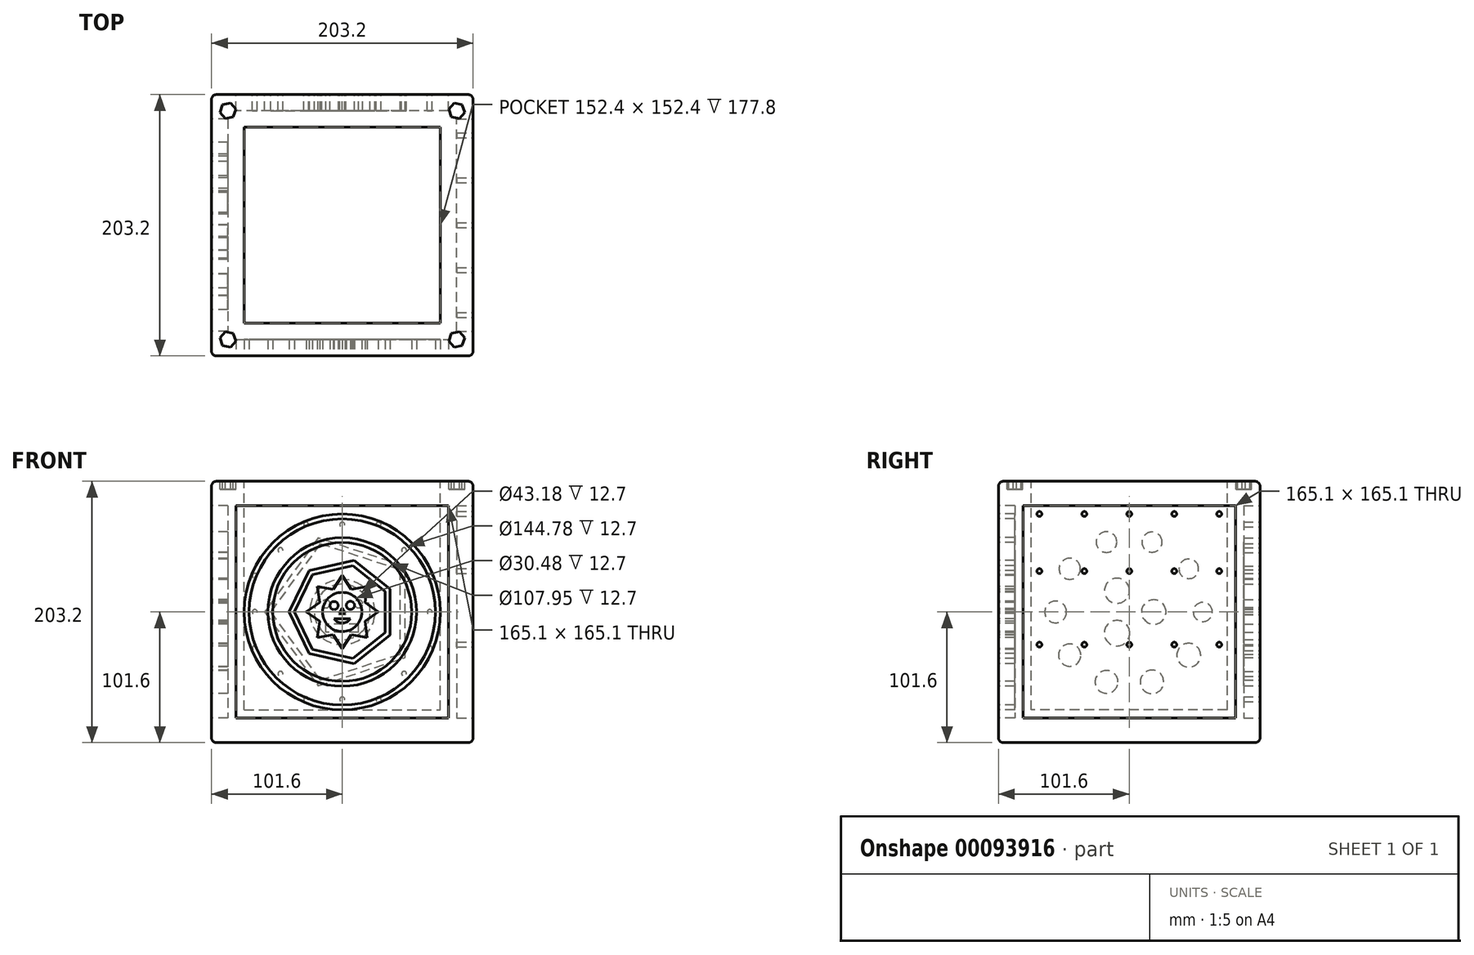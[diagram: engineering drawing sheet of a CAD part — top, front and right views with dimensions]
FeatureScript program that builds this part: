
annotation { "Feature Type Name" : "Feature", "Feature Type Description" : "" }
export const myFeature = defineFeature(function(context is Context, id is Id, definition is map)
    precondition{}
    {
        {
            var Q0;
            Q0=qCreatedBy(makeId("Front.planeOp"),FACE);
            var sketch = newSketch(context, id + "F0", { "sketchPlane" : qUnion([Q0])});
            skLineSegment(sketch, "E0.bottom", {"start": v(-101.6, 101.6) * mm, "end": v(101.6, 101.6) * mm});
            skLineSegment(sketch, "E0.top", {"start": v(-101.6, -101.6) * mm, "end": v(101.6, -101.6) * mm});
            skLineSegment(sketch, "E0.left", {"start": v(-101.6, 101.6) * mm, "end": v(-101.6, -101.6) * mm});
            skLineSegment(sketch, "E0.right", {"start": v(101.6, 101.6) * mm, "end": v(101.6, -101.6) * mm});
            skPoint(sketch, "E0.middle", {"position": v(0, 0) * mm});
            skSolve(sketch);
        }
        {
            var Q0;
            Q0 = qSketchRegion(id + "F0", true);
            extrude(context, id + "F1", {"entities" : qUnion([Q0]), "endBound" : BoundingType.SYMMETRIC, "depth" : 203.2 * mm});
        }
        {
            var Q0;
            Q0=makeQuery(id+"F1.opExtrude","SWEPT_FACE",FACE,{"disambiguationData":[OSD([sQuery(id+"F0.wireOp",EDGE,"E0.bottom")])]});
            var sketch = newSketch(context, id + "F2", { "sketchPlane" : qUnion([Q0])});
            skPoint(sketch, "E1.middle", {"position": v(0, 0) * mm});
            skLineSegment(sketch, "E2.bottom", {"start": v(-76.2, 76.2) * mm, "end": v(76.2, 76.2) * mm});
            skLineSegment(sketch, "E2.top", {"start": v(-76.2, -76.2) * mm, "end": v(76.2, -76.2) * mm});
            skLineSegment(sketch, "E2.left", {"start": v(-76.2, 76.2) * mm, "end": v(-76.2, -76.2) * mm});
            skLineSegment(sketch, "E2.right", {"start": v(76.2, 76.2) * mm, "end": v(76.2, -76.2) * mm});
            skLineSegment(sketch, "E3.bottom", {"start": v(-76.2, 76.2) * mm, "end": v(-101.6, 76.2) * mm, "construction": true});
            skLineSegment(sketch, "E3.top", {"start": v(-76.2, 101.6) * mm, "end": v(-101.6, 101.6) * mm, "construction": true});
            skLineSegment(sketch, "E3.left", {"start": v(-76.2, 76.2) * mm, "end": v(-76.2, 101.6) * mm, "construction": true});
            skLineSegment(sketch, "E3.right", {"start": v(-101.6, 76.2) * mm, "end": v(-101.6, 101.6) * mm, "construction": true});
            skLineSegment(sketch, "E4.bottom", {"start": v(76.2, 76.2) * mm, "end": v(101.6, 76.2) * mm, "construction": true});
            skLineSegment(sketch, "E4.top", {"start": v(76.2, 101.6) * mm, "end": v(101.6, 101.6) * mm, "construction": true});
            skLineSegment(sketch, "E4.left", {"start": v(76.2, 76.2) * mm, "end": v(76.2, 101.6) * mm, "construction": true});
            skLineSegment(sketch, "E4.right", {"start": v(101.6, 76.2) * mm, "end": v(101.6, 101.6) * mm, "construction": true});
            skLineSegment(sketch, "E5.bottom", {"start": v(-76.2, -76.2) * mm, "end": v(-101.6, -76.2) * mm, "construction": true});
            skLineSegment(sketch, "E5.top", {"start": v(-76.2, -101.6) * mm, "end": v(-101.6, -101.6) * mm, "construction": true});
            skLineSegment(sketch, "E5.left", {"start": v(-76.2, -76.2) * mm, "end": v(-76.2, -101.6) * mm, "construction": true});
            skLineSegment(sketch, "E5.right", {"start": v(-101.6, -76.2) * mm, "end": v(-101.6, -101.6) * mm, "construction": true});
            skLineSegment(sketch, "E6.bottom", {"start": v(76.2, -76.2) * mm, "end": v(101.6, -76.2) * mm, "construction": true});
            skLineSegment(sketch, "E6.top", {"start": v(76.2, -101.6) * mm, "end": v(101.6, -101.6) * mm, "construction": true});
            skLineSegment(sketch, "E6.left", {"start": v(76.2, -76.2) * mm, "end": v(76.2, -101.6) * mm, "construction": true});
            skLineSegment(sketch, "E6.right", {"start": v(101.6, -76.2) * mm, "end": v(101.6, -101.6) * mm, "construction": true});
            skLineSegment(sketch, "E7", {"start": v(-101.6, 76.2) * mm, "end": v(-76.2, 101.6) * mm, "construction": true});
            skCircle(sketch, "E8.cCircle", {"center": v(-88.9, 88.9) * mm, "radius": 5.5 * mm, "construction": true});
            skLineSegment(sketch, "E8.0", {"start": v(-84.72, 84.12) * mm, "end": v(-90.95, 82.9) * mm});
            skLineSegment(sketch, "E8.1", {"start": v(-90.95, 82.9) * mm, "end": v(-95.13, 87.68) * mm});
            skLineSegment(sketch, "E8.2", {"start": v(-95.13, 87.68) * mm, "end": v(-93.08, 93.68) * mm});
            skLineSegment(sketch, "E8.3", {"start": v(-93.08, 93.68) * mm, "end": v(-86.85, 94.9) * mm});
            skLineSegment(sketch, "E8.4", {"start": v(-86.85, 94.9) * mm, "end": v(-82.67, 90.12) * mm});
            skLineSegment(sketch, "E8.5", {"start": v(-82.67, 90.12) * mm, "end": v(-84.72, 84.12) * mm});
            skPoint(sketch, "E8.0.midPoint", {"position": v(-87.84, 83.5) * mm});
            skLineSegment(sketch, "E9", {"start": v(0, 101.6) * mm, "end": v(0, -101.6) * mm, "construction": true});
            skLineSegment(sketch, "E10", {"start": v(-101.6, 0) * mm, "end": v(101.6, 0) * mm, "construction": true});
            skLineSegment(sketch, "E11.MirrorCS", {"start": v(0, -101.6) * mm, "end": v(0, 101.6) * mm, "construction": true});
            skLineSegment(sketch, "E12.MirrorCS", {"start": v(-90.95, -82.9) * mm, "end": v(-95.13, -87.68) * mm});
            skLineSegment(sketch, "E13.MirrorCS", {"start": v(-95.13, -87.68) * mm, "end": v(-93.08, -93.68) * mm});
            skLineSegment(sketch, "E14.MirrorCS", {"start": v(-93.08, -93.68) * mm, "end": v(-86.85, -94.9) * mm});
            skLineSegment(sketch, "E15.MirrorCS", {"start": v(-86.85, -94.9) * mm, "end": v(-82.67, -90.12) * mm});
            skLineSegment(sketch, "E16.MirrorCS", {"start": v(-82.67, -90.12) * mm, "end": v(-84.72, -84.12) * mm});
            skLineSegment(sketch, "E17.MirrorCS", {"start": v(-84.72, -84.12) * mm, "end": v(-90.95, -82.9) * mm});
            skLineSegment(sketch, "E18.MirrorCS", {"start": v(82.67, 90.12) * mm, "end": v(84.72, 84.12) * mm});
            skLineSegment(sketch, "E19.MirrorCS", {"start": v(86.85, 94.9) * mm, "end": v(82.67, 90.12) * mm});
            skLineSegment(sketch, "E20.MirrorCS", {"start": v(93.08, 93.68) * mm, "end": v(86.85, 94.9) * mm});
            skLineSegment(sketch, "E21.MirrorCS", {"start": v(95.13, 87.68) * mm, "end": v(93.08, 93.68) * mm});
            skLineSegment(sketch, "E22.MirrorCS", {"start": v(90.95, 82.9) * mm, "end": v(95.13, 87.68) * mm});
            skLineSegment(sketch, "E23.MirrorCS", {"start": v(84.72, 84.12) * mm, "end": v(90.95, 82.9) * mm});
            skLineSegment(sketch, "E24.MirrorCS", {"start": v(82.67, -90.12) * mm, "end": v(84.72, -84.12) * mm});
            skLineSegment(sketch, "E25.MirrorCS", {"start": v(84.72, -84.12) * mm, "end": v(90.95, -82.9) * mm});
            skLineSegment(sketch, "E26.MirrorCS", {"start": v(90.95, -82.9) * mm, "end": v(95.13, -87.68) * mm});
            skLineSegment(sketch, "E27.MirrorCS", {"start": v(95.13, -87.68) * mm, "end": v(93.08, -93.68) * mm});
            skLineSegment(sketch, "E28.MirrorCS", {"start": v(93.08, -93.68) * mm, "end": v(86.85, -94.9) * mm});
            skLineSegment(sketch, "E29.MirrorCS", {"start": v(86.85, -94.9) * mm, "end": v(82.67, -90.12) * mm});
            skSolve(sketch);
        }
        {
            var Q0;
            Q0=makeQuery(id+"F2.imprint","IMPRINT",FACE,{"disambiguationData":[TD([[makeQuery(id+"F2.imprint","IMPRINT",EDGE,{"derivedFrom":sQuery(id+"F2.wireOp",EDGE,"E2.bottom")}),-1.0]])]});
            extrude(context, id + "F3", {"entities" : qUnion([Q0]), "operationType" : NewBodyOperationType.REMOVE, "oppositeDirection" : true, "depth" : 177.8 * mm});
        }
        {
            var Q0;
            Q0=makeQuery(id+"F1.opExtrude","SWEPT_FACE",FACE,{"disambiguationData":[OSD([sQuery(id+"F0.wireOp",EDGE,"E0.right")])]});
            var sketch = newSketch(context, id + "F4", { "sketchPlane" : qUnion([Q0])});
            skLineSegment(sketch, "E30.bottom", {"start": v(-101.6, 101.6) * mm, "end": v(101.6, 101.6) * mm});
            skLineSegment(sketch, "E30.top", {"start": v(-101.6, -101.6) * mm, "end": v(101.6, -101.6) * mm});
            skLineSegment(sketch, "E30.left", {"start": v(-101.6, 101.6) * mm, "end": v(-101.6, -101.6) * mm});
            skLineSegment(sketch, "E31.0", {"start": v(-82.55, 82.55) * mm, "end": v(-82.55, -82.55) * mm});
            skLineSegment(sketch, "E31.1", {"start": v(-82.55, 82.55) * mm, "end": v(82.55, 82.55) * mm});
            skLineSegment(sketch, "E31.3", {"start": v(-82.55, -82.55) * mm, "end": v(82.55, -82.55) * mm});
            skCircle(sketch, "E32", {"center": v(-69.85, 76.2) * mm, "radius": 1.9 * mm});
            skCircle(sketch, "E33", {"center": v(-69.85, 31.75) * mm, "radius": 1.9 * mm});
            skCircle(sketch, "E34", {"center": v(-69.85, -25.4) * mm, "radius": 1.9 * mm});
            skCircle(sketch, "E35.1.0.0", {"center": v(-34.93, 76.2) * mm, "radius": 1.9 * mm});
            skCircle(sketch, "E35.1.0.1", {"center": v(-34.93, 31.75) * mm, "radius": 1.9 * mm});
            skCircle(sketch, "E35.1.0.2", {"center": v(-34.92, -25.4) * mm, "radius": 1.9 * mm});
            skCircle(sketch, "E35.2.0.0", {"center": v(0, 76.2) * mm, "radius": 1.9 * mm});
            skCircle(sketch, "E35.2.0.1", {"center": v(0, 31.75) * mm, "radius": 1.9 * mm});
            skCircle(sketch, "E35.2.0.2", {"center": v(0, -25.4) * mm, "radius": 1.9 * mm});
            skCircle(sketch, "E35.3.0.0", {"center": v(34.93, 76.2) * mm, "radius": 1.9 * mm});
            skCircle(sketch, "E35.3.0.1", {"center": v(34.93, 31.75) * mm, "radius": 1.9 * mm});
            skCircle(sketch, "E35.3.0.2", {"center": v(34.93, -25.4) * mm, "radius": 1.9 * mm});
            skCircle(sketch, "E35.4.0.0", {"center": v(69.85, 76.2) * mm, "radius": 1.9 * mm});
            skCircle(sketch, "E35.4.0.1", {"center": v(69.85, 31.75) * mm, "radius": 1.9 * mm});
            skCircle(sketch, "E35.4.0.2", {"center": v(69.85, -25.4) * mm, "radius": 1.9 * mm});
            skLineSegment(sketch, "E35.direction1", {"start": v(-69.85, 76.2) * mm, "end": v(-34.93, 76.2) * mm, "construction": true});
            skLineSegment(sketch, "E36", {"start": v(101.6, 101.6) * mm, "end": v(101.6, -101.6) * mm});
            skLineSegment(sketch, "E37.0", {"start": v(82.55, 82.55) * mm, "end": v(82.55, -82.55) * mm});
            skSolve(sketch);
        }
        {
            var Q0;
            Q0=makeQuery(id+"F4.imprint","IMPRINT",FACE,{"disambiguationData":[TD([[makeQuery(id+"F4.imprint","IMPRINT",EDGE,{"derivedFrom":sQuery(id+"F4.wireOp",EDGE,"E31.0")}),1.0]])]});
            extrude(context, id + "F5", {"entities" : qUnion([Q0]), "operationType" : NewBodyOperationType.REMOVE, "oppositeDirection" : true, "depth" : 12.7 * mm});
        }
        {
            var Q0;
            Q0=makeQuery(id+"F1.opExtrude","CAP_FACE",FACE,{"disambiguationData":[OSD([sQuery(id+"F0.wireOp",EDGE,"E0.bottom"),sQuery(id+"F0.wireOp",EDGE,"E0.top"),sQuery(id+"F0.wireOp",EDGE,"E0.left"),sQuery(id+"F0.wireOp",EDGE,"E0.right")])],"isStart":false});
            var sketch = newSketch(context, id + "F6", { "sketchPlane" : qUnion([Q0])});
            skLineSegment(sketch, "E38.bottom", {"start": v(-101.6, 101.6) * mm, "end": v(101.6, 101.6) * mm});
            skLineSegment(sketch, "E38.top", {"start": v(-101.6, -101.6) * mm, "end": v(101.6, -101.6) * mm});
            skLineSegment(sketch, "E38.left", {"start": v(-101.6, 101.6) * mm, "end": v(-101.6, -101.6) * mm});
            skLineSegment(sketch, "E38.right", {"start": v(101.6, 101.6) * mm, "end": v(101.6, -101.6) * mm});
            skPoint(sketch, "E38.middle", {"position": v(0, 0) * mm});
            skLineSegment(sketch, "E39.0", {"start": v(-82.55, 82.55) * mm, "end": v(-82.55, -82.55) * mm});
            skLineSegment(sketch, "E39.1", {"start": v(-82.55, 82.55) * mm, "end": v(82.55, 82.55) * mm});
            skLineSegment(sketch, "E39.2", {"start": v(82.55, 82.55) * mm, "end": v(82.55, -82.55) * mm});
            skLineSegment(sketch, "E39.3", {"start": v(-82.55, -82.55) * mm, "end": v(82.55, -82.55) * mm});
            skCircle(sketch, "E40", {"center": v(0, 0) * mm, "radius": 76.2 * mm});
            skCircle(sketch, "E41.0", {"center": v(0, 0) * mm, "radius": 57.79 * mm});
            skCircle(sketch, "E42.0", {"center": v(0, 0) * mm, "radius": 53.98 * mm});
            skCircle(sketch, "E43.cCircle", {"center": v(0, 0) * mm, "radius": 53.98 * mm, "construction": true});
            skCircle(sketch, "E44.cCircle", {"center": v(0, 0) * mm, "radius": 41.28 * mm, "construction": true});
            skLineSegment(sketch, "E44.0", {"start": v(-41.28, 0) * mm, "end": v(-25.73, 32.27) * mm});
            skLineSegment(sketch, "E44.1", {"start": v(-25.73, 32.27) * mm, "end": v(9.18, 40.24) * mm});
            skLineSegment(sketch, "E44.2", {"start": v(9.18, 40.24) * mm, "end": v(37.19, 17.9) * mm});
            skLineSegment(sketch, "E44.3", {"start": v(37.19, 17.9) * mm, "end": v(37.19, -17.9) * mm});
            skLineSegment(sketch, "E44.4", {"start": v(37.19, -17.9) * mm, "end": v(9.18, -40.24) * mm});
            skLineSegment(sketch, "E44.5", {"start": v(9.18, -40.24) * mm, "end": v(-25.73, -32.27) * mm});
            skLineSegment(sketch, "E44.6", {"start": v(-25.73, -32.27) * mm, "end": v(-41.28, 0) * mm});
            skLineSegment(sketch, "E45.0", {"start": v(-23.1, -28.96) * mm, "end": v(-37.05, 0) * mm});
            skLineSegment(sketch, "E45.1", {"start": v(8.24, -36.12) * mm, "end": v(-23.1, -28.96) * mm});
            skLineSegment(sketch, "E45.2", {"start": v(-23.1, 28.96) * mm, "end": v(8.24, 36.12) * mm});
            skLineSegment(sketch, "E45.3", {"start": v(8.24, 36.12) * mm, "end": v(33.38, 16.07) * mm});
            skLineSegment(sketch, "E45.4", {"start": v(33.38, 16.07) * mm, "end": v(33.38, -16.07) * mm});
            skLineSegment(sketch, "E45.5", {"start": v(-37.05, 0) * mm, "end": v(-23.1, 28.96) * mm});
            skLineSegment(sketch, "E45.6", {"start": v(33.38, -16.07) * mm, "end": v(8.24, -36.12) * mm});
            skCircle(sketch, "E46.0", {"center": v(0, 0) * mm, "radius": 72.4 * mm});
            skCircle(sketch, "E47", {"center": v(0, 0) * mm, "radius": 19.05 * mm});
            skLineSegment(sketch, "E48", {"start": v(-28, 0) * mm, "end": v(29.66, 0) * mm, "construction": true});
            skLineSegment(sketch, "E49", {"start": v(-19.48, 19.85) * mm, "end": v(-17.6, 7.29) * mm});
            skLineSegment(sketch, "E50.MirrorCS", {"start": v(-19.48, 19.85) * mm, "end": v(-6.96, 17.73) * mm});
            skLineSegment(sketch, "E51", {"start": v(0, 28.36) * mm, "end": v(-6.96, 17.73) * mm});
            skLineSegment(sketch, "E52", {"start": v(-17.6, 7.29) * mm, "end": v(-28, 0) * mm});
            skLineSegment(sketch, "E53", {"start": v(0, 28.36) * mm, "end": v(6.96, 17.73) * mm});
            skLineSegment(sketch, "E54", {"start": v(6.96, 17.73) * mm, "end": v(19.47, 19.9) * mm});
            skLineSegment(sketch, "E55", {"start": v(19.47, 19.9) * mm, "end": v(17.58, 7.33) * mm});
            skLineSegment(sketch, "E56", {"start": v(17.58, 7.33) * mm, "end": v(27.95, 0) * mm});
            skLineSegment(sketch, "E57.MirrorCS", {"start": v(-17.6, -7.29) * mm, "end": v(-28, 0) * mm});
            skLineSegment(sketch, "E58.MirrorCS", {"start": v(-19.48, -19.85) * mm, "end": v(-17.6, -7.29) * mm});
            skLineSegment(sketch, "E59.MirrorCS", {"start": v(-19.48, -19.85) * mm, "end": v(-6.96, -17.73) * mm});
            skLineSegment(sketch, "E60.MirrorCS", {"start": v(0, -28.36) * mm, "end": v(-6.96, -17.73) * mm});
            skLineSegment(sketch, "E61.MirrorCS", {"start": v(0, -28.36) * mm, "end": v(6.96, -17.73) * mm});
            skLineSegment(sketch, "E62.MirrorCS", {"start": v(6.96, -17.73) * mm, "end": v(19.47, -19.9) * mm});
            skLineSegment(sketch, "E63.MirrorCS", {"start": v(19.47, -19.9) * mm, "end": v(17.58, -7.33) * mm});
            skLineSegment(sketch, "E64.MirrorCS", {"start": v(17.58, -7.33) * mm, "end": v(27.95, 0) * mm});
            skCircle(sketch, "E65.0", {"center": v(0, 0) * mm, "radius": 15.24 * mm});
            skCircle(sketch, "E66", {"center": v(-6.38, 5.04) * mm, "radius": 3.18 * mm});
            skCircle(sketch, "E67", {"center": v(6.32, 5.12) * mm, "radius": 3.18 * mm});
            skCircle(sketch, "E68.cCircle", {"center": v(0, 0) * mm, "radius": 1.26 * mm, "construction": true});
            skLineSegment(sketch, "E68.0", {"start": v(-2.19, -1.26) * mm, "end": v(0, 2.53) * mm});
            skLineSegment(sketch, "E68.1", {"start": v(0, 2.53) * mm, "end": v(2.19, -1.26) * mm});
            skLineSegment(sketch, "E68.2", {"start": v(2.19, -1.26) * mm, "end": v(-2.19, -1.26) * mm});
            skPoint(sketch, "E68.0.midPoint", {"position": v(-1.1, 0.63) * mm});
            skLineSegment(sketch, "E69", {"start": v(-6.38, -5.21) * mm, "end": v(6.32, -5.21) * mm});
            skArc(sketch, "E70", {"start": v(-6.38, -5.21) * mm, "mid": v(-0.03, -8.62) * mm, "end": v(6.32, -5.21) * mm});
            skSolve(sketch);
        }
        {
            var Q0;
            Q0=makeQuery(id+"F6.imprint","IMPRINT",FACE,{"disambiguationData":[TD([[makeQuery(id+"F6.imprint","IMPRINT",EDGE,{"derivedFrom":sQuery(id+"F6.wireOp",EDGE,"E42.0")}),1.0]])]});
            extrude(context, id + "F7", {"entities" : qUnion([Q0]), "operationType" : NewBodyOperationType.REMOVE, "oppositeDirection" : true, "depth" : 12.7 * mm});
        }
        {
            var Q0;
            Q0=makeQuery(id+"F6.imprint","IMPRINT",FACE,{"disambiguationData":[TD([[makeQuery(id+"F6.imprint","IMPRINT",EDGE,{"derivedFrom":sQuery(id+"F6.wireOp",EDGE,"E39.0")}),1.0]])]});
            extrude(context, id + "F8", {"entities" : qUnion([Q0]), "operationType" : NewBodyOperationType.REMOVE, "oppositeDirection" : true, "depth" : 12.7 * mm});
        }
        {
            var Q0;
            Q0=makeQuery(id+"F1.opExtrude","SWEPT_FACE",FACE,{"disambiguationData":[OSD([sQuery(id+"F0.wireOp",EDGE,"E0.left")])]});
            var sketch = newSketch(context, id + "F9", { "sketchPlane" : qUnion([Q0])});
            skLineSegment(sketch, "E71.bottom", {"start": v(-101.6, 101.6) * mm, "end": v(101.6, 101.6) * mm});
            skLineSegment(sketch, "E71.top", {"start": v(-101.6, -101.6) * mm, "end": v(101.6, -101.6) * mm});
            skLineSegment(sketch, "E71.left", {"start": v(-101.6, 101.6) * mm, "end": v(-101.6, -101.6) * mm});
            skLineSegment(sketch, "E71.right", {"start": v(101.6, 101.6) * mm, "end": v(101.6, -101.6) * mm});
            skPoint(sketch, "E71.middle", {"position": v(0, 0) * mm});
            skLineSegment(sketch, "E72.0", {"start": v(-82.55, 82.55) * mm, "end": v(-82.55, -82.55) * mm});
            skLineSegment(sketch, "E72.1", {"start": v(-82.55, 82.55) * mm, "end": v(82.55, 82.55) * mm});
            skLineSegment(sketch, "E72.2", {"start": v(82.55, 82.55) * mm, "end": v(82.55, -82.55) * mm});
            skLineSegment(sketch, "E72.3", {"start": v(-82.55, -82.55) * mm, "end": v(82.55, -82.55) * mm});
            skCircle(sketch, "E73.cCircle", {"center": v(0, 0) * mm, "radius": 57.15 * mm, "construction": true});
            skPoint(sketch, "E73.cCircle.perimeterSnap0", {"position": v(-82.55, 0) * mm});
            skLineSegment(sketch, "E73.0", {"start": v(-57.15, -18.57) * mm, "end": v(-57.15, 18.57) * mm, "construction": true});
            skLineSegment(sketch, "E73.1", {"start": v(-57.15, 18.57) * mm, "end": v(-35.32, 48.61) * mm, "construction": true});
            skLineSegment(sketch, "E73.2", {"start": v(-35.32, 48.61) * mm, "end": v(0, 60.1) * mm, "construction": true});
            skLineSegment(sketch, "E73.3", {"start": v(0, 60.1) * mm, "end": v(35.32, 48.61) * mm, "construction": true});
            skLineSegment(sketch, "E73.4", {"start": v(35.32, 48.61) * mm, "end": v(57.15, 18.57) * mm, "construction": true});
            skLineSegment(sketch, "E73.5", {"start": v(57.15, 18.57) * mm, "end": v(57.15, -18.57) * mm, "construction": true});
            skLineSegment(sketch, "E73.6", {"start": v(57.15, -18.57) * mm, "end": v(35.32, -48.61) * mm, "construction": true});
            skLineSegment(sketch, "E73.7", {"start": v(35.32, -48.61) * mm, "end": v(0, -60.1) * mm, "construction": true});
            skLineSegment(sketch, "E73.8", {"start": v(0, -60.1) * mm, "end": v(-35.32, -48.61) * mm, "construction": true});
            skLineSegment(sketch, "E73.9", {"start": v(-35.32, -48.61) * mm, "end": v(-57.15, -18.57) * mm, "construction": true});
            skPoint(sketch, "E73.0.midPoint", {"position": v(-57.15, 0) * mm});
            skPoint(sketch, "E73.0.midPoint.positionSnap0", {"position": v(-82.55, 0) * mm});
            skCircle(sketch, "E74", {"center": v(-57.15, 0) * mm, "radius": 7.43 * mm});
            skCircle(sketch, "E75", {"center": v(-46.24, 33.6) * mm, "radius": 7.63 * mm});
            skCircle(sketch, "E76", {"center": v(-17.66, 54.35) * mm, "radius": 7.85 * mm});
            skCircle(sketch, "E77", {"center": v(17.66, 54.35) * mm, "radius": 8.05 * mm});
            skCircle(sketch, "E78", {"center": v(46.24, 33.6) * mm, "radius": 8.26 * mm});
            skCircle(sketch, "E79", {"center": v(57.15, 0) * mm, "radius": 8.46 * mm});
            skCircle(sketch, "E80", {"center": v(46.24, -33.6) * mm, "radius": 8.67 * mm});
            skCircle(sketch, "E81", {"center": v(17.66, -54.35) * mm, "radius": 8.88 * mm});
            skCircle(sketch, "E82", {"center": v(-17.66, -54.35) * mm, "radius": 9.1 * mm});
            skCircle(sketch, "E83", {"center": v(-46.24, -33.6) * mm, "radius": 9.26 * mm});
            skCircle(sketch, "E84.cCircle", {"center": v(0, 0) * mm, "radius": 19.05 * mm, "construction": true});
            skLineSegment(sketch, "E84.0", {"start": v(-19.05, -33) * mm, "end": v(-19.05, 33) * mm, "construction": true});
            skLineSegment(sketch, "E84.1", {"start": v(-19.05, 33) * mm, "end": v(38.1, 0) * mm, "construction": true});
            skLineSegment(sketch, "E84.2", {"start": v(38.1, 0) * mm, "end": v(-19.05, -33) * mm, "construction": true});
            skPoint(sketch, "E84.0.midPoint", {"position": v(-19.05, 0) * mm});
            skCircle(sketch, "E85", {"center": v(-19.05, 0) * mm, "radius": 9.5 * mm});
            skCircle(sketch, "E86", {"center": v(9.53, 16.5) * mm, "radius": 9.7 * mm});
            skCircle(sketch, "E87", {"center": v(9.53, -16.5) * mm, "radius": 9.92 * mm});
            skSolve(sketch);
        }
        {
            var Q0;
            Q0=makeQuery(id+"F9.imprint","IMPRINT",FACE,{"disambiguationData":[TD([[makeQuery(id+"F9.imprint","IMPRINT",EDGE,{"derivedFrom":sQuery(id+"F9.wireOp",EDGE,"E72.0")}),1.0]])]});
            extrude(context, id + "F10", {"entities" : qUnion([Q0]), "operationType" : NewBodyOperationType.REMOVE, "oppositeDirection" : true, "depth" : 12.7 * mm});
        }
        {
            var Q0;
            Q0=makeQuery(id+"F1.opExtrude","CAP_FACE",FACE,{"disambiguationData":[OSD([sQuery(id+"F0.wireOp",EDGE,"E0.bottom"),sQuery(id+"F0.wireOp",EDGE,"E0.top"),sQuery(id+"F0.wireOp",EDGE,"E0.left"),sQuery(id+"F0.wireOp",EDGE,"E0.right")])],"isStart":true});
            var sketch = newSketch(context, id + "F11", { "sketchPlane" : qUnion([Q0])});
            skLineSegment(sketch, "E88.bottom", {"start": v(-101.6, 101.6) * mm, "end": v(101.6, 101.6) * mm});
            skLineSegment(sketch, "E88.top", {"start": v(-101.6, -101.6) * mm, "end": v(101.6, -101.6) * mm});
            skLineSegment(sketch, "E88.left", {"start": v(-101.6, 101.6) * mm, "end": v(-101.6, -101.6) * mm});
            skLineSegment(sketch, "E88.right", {"start": v(101.6, 101.6) * mm, "end": v(101.6, -101.6) * mm});
            skPoint(sketch, "E88.middle", {"position": v(0, 0) * mm});
            skLineSegment(sketch, "E89.0", {"start": v(-82.55, 82.55) * mm, "end": v(-82.55, -82.55) * mm});
            skLineSegment(sketch, "E89.1", {"start": v(-82.55, 82.55) * mm, "end": v(82.55, 82.55) * mm});
            skLineSegment(sketch, "E89.2", {"start": v(82.55, 82.55) * mm, "end": v(82.55, -82.55) * mm});
            skLineSegment(sketch, "E89.3", {"start": v(-82.55, -82.55) * mm, "end": v(82.55, -82.55) * mm});
            skCircle(sketch, "E90.cCircle", {"center": v(0, 0) * mm, "radius": 67.95 * mm, "construction": true});
            skPoint(sketch, "E90.cCircle.perimeterSnap0", {"position": v(-82.55, 0) * mm});
            skPoint(sketch, "E90.0.midPoint", {"position": v(-67.95, 0) * mm});
            skPoint(sketch, "E90.0.midPoint.positionSnap0", {"position": v(-82.55, 0) * mm});
            skLineSegment(sketch, "E91", {"start": v(-28.93, 69.85) * mm, "end": v(-27.35, 66.04) * mm});
            skLineSegment(sketch, "E92", {"start": v(28.93, 69.85) * mm, "end": v(27.35, 66.04) * mm});
            skLineSegment(sketch, "E93", {"start": v(69.85, 28.93) * mm, "end": v(66.04, 27.35) * mm});
            skLineSegment(sketch, "E94", {"start": v(69.85, -28.93) * mm, "end": v(66.04, -27.35) * mm});
            skLineSegment(sketch, "E95", {"start": v(28.93, -69.85) * mm, "end": v(27.35, -66.04) * mm});
            skLineSegment(sketch, "E96", {"start": v(-28.93, -69.85) * mm, "end": v(-27.35, -66.04) * mm});
            skLineSegment(sketch, "E97", {"start": v(-69.85, -28.93) * mm, "end": v(-66.04, -27.35) * mm});
            skLineSegment(sketch, "E98", {"start": v(-69.85, 28.93) * mm, "end": v(-66.04, 27.35) * mm});
            skLineSegment(sketch, "E99", {"start": v(-67.95, 28.14) * mm, "end": v(-28.14, 67.95) * mm, "construction": true});
            skLineSegment(sketch, "E100", {"start": v(-28.14, 67.95) * mm, "end": v(28.14, 67.95) * mm, "construction": true});
            skLineSegment(sketch, "E101", {"start": v(28.14, 67.95) * mm, "end": v(67.95, 28.14) * mm, "construction": true});
            skLineSegment(sketch, "E102", {"start": v(67.95, 28.14) * mm, "end": v(67.94, -28.14) * mm, "construction": true});
            skLineSegment(sketch, "E103", {"start": v(67.94, -28.14) * mm, "end": v(28.14, -67.95) * mm, "construction": true});
            skLineSegment(sketch, "E104", {"start": v(28.14, -67.95) * mm, "end": v(-28.14, -67.95) * mm, "construction": true});
            skPoint(sketch, "E105.endSnap0", {"position": v(-67.95, -28.14) * mm});
            skLineSegment(sketch, "E106", {"start": v(-28.14, -67.95) * mm, "end": v(-67.95, -28.14) * mm, "construction": true});
            skLineSegment(sketch, "E107", {"start": v(-67.95, -28.14) * mm, "end": v(-67.95, 28.14) * mm, "construction": true});
            skCircle(sketch, "E108", {"center": v(-67.95, -28.14) * mm, "radius": 1.9 * mm});
            skCircle(sketch, "E109", {"center": v(-67.95, 0) * mm, "radius": 1.9 * mm});
            skCircle(sketch, "E110", {"center": v(-67.95, 28.14) * mm, "radius": 1.9 * mm});
            skCircle(sketch, "E111", {"center": v(-48.04, 48.04) * mm, "radius": 1.9 * mm});
            skCircle(sketch, "E112", {"center": v(-28.14, 67.95) * mm, "radius": 1.9 * mm});
            skCircle(sketch, "E113", {"center": v(0, 67.95) * mm, "radius": 1.9 * mm});
            skCircle(sketch, "E114", {"center": v(28.14, 67.95) * mm, "radius": 1.9 * mm});
            skCircle(sketch, "E115", {"center": v(-48.04, -48.04) * mm, "radius": 1.9 * mm});
            skCircle(sketch, "E116", {"center": v(-28.14, -67.95) * mm, "radius": 1.9 * mm});
            skCircle(sketch, "E117", {"center": v(0, -67.95) * mm, "radius": 1.9 * mm});
            skCircle(sketch, "E118", {"center": v(28.14, -67.95) * mm, "radius": 1.9 * mm});
            skCircle(sketch, "E119", {"center": v(48.04, -48.04) * mm, "radius": 1.9 * mm});
            skCircle(sketch, "E120", {"center": v(67.95, -28.14) * mm, "radius": 1.9 * mm});
            skCircle(sketch, "E121", {"center": v(67.95, 0) * mm, "radius": 1.9 * mm});
            skCircle(sketch, "E122", {"center": v(67.95, 28.14) * mm, "radius": 1.9 * mm});
            skCircle(sketch, "E123", {"center": v(48.04, 48.04) * mm, "radius": 1.9 * mm});
            skCircle(sketch, "E124.cCircle", {"center": v(0, 0) * mm, "radius": 48.9 * mm, "construction": true});
            skLineSegment(sketch, "E124.0", {"start": v(-48.9, -35.52) * mm, "end": v(-48.9, 35.52) * mm});
            skLineSegment(sketch, "E124.1", {"start": v(-48.9, 35.52) * mm, "end": v(18.68, 57.48) * mm});
            skLineSegment(sketch, "E124.2", {"start": v(18.68, 57.48) * mm, "end": v(60.44, 0) * mm});
            skLineSegment(sketch, "E124.3", {"start": v(60.44, 0) * mm, "end": v(18.68, -57.48) * mm});
            skLineSegment(sketch, "E124.4", {"start": v(18.68, -57.48) * mm, "end": v(-48.9, -35.52) * mm});
            skPoint(sketch, "E124.0.midPoint", {"position": v(-48.9, 0) * mm});
            skLineSegment(sketch, "E125.0", {"start": v(-45.09, 32.76) * mm, "end": v(17.22, 53) * mm});
            skLineSegment(sketch, "E125.1", {"start": v(-45.09, -32.76) * mm, "end": v(-45.09, 32.76) * mm});
            skLineSegment(sketch, "E125.2", {"start": v(17.22, 53) * mm, "end": v(55.73, 0) * mm});
            skLineSegment(sketch, "E125.3", {"start": v(55.73, 0) * mm, "end": v(17.22, -53) * mm});
            skLineSegment(sketch, "E125.4", {"start": v(17.22, -53) * mm, "end": v(-45.09, -32.76) * mm});
            skCircle(sketch, "E126", {"center": v(0, 0) * mm, "radius": 25.4 * mm});
            skCircle(sketch, "E127", {"center": v(-12.7, 6.35) * mm, "radius": 3.18 * mm});
            skCircle(sketch, "E128", {"center": v(12.7, 6.35) * mm, "radius": 3.18 * mm});
            skLineSegment(sketch, "E129.bottom", {"start": v(-12.7, -15.88) * mm, "end": v(12.7, -15.88) * mm});
            skLineSegment(sketch, "E129.top", {"start": v(-12.7, -9.53) * mm, "end": v(12.7, -9.53) * mm});
            skLineSegment(sketch, "E129.left", {"start": v(-12.7, -15.88) * mm, "end": v(-12.7, -9.53) * mm});
            skLineSegment(sketch, "E129.right", {"start": v(12.7, -15.88) * mm, "end": v(12.7, -9.53) * mm});
            skPoint(sketch, "E129.middle", {"position": v(0, -12.7) * mm});
            skLineSegment(sketch, "E130", {"start": v(-2.87, -2.05) * mm, "end": v(0, 3.62) * mm});
            skLineSegment(sketch, "E131", {"start": v(0, 3.62) * mm, "end": v(2.87, -2.05) * mm});
            skLineSegment(sketch, "E132", {"start": v(-2.87, -2.05) * mm, "end": v(2.87, -2.05) * mm});
            skCircle(sketch, "E133.0", {"center": v(0, 0) * mm, "radius": 21.59 * mm});
            skSolve(sketch);
        }
        {
            var Q0;
            Q0=makeQuery(id+"F11.imprint","IMPRINT",FACE,{"disambiguationData":[TD([[makeQuery(id+"F11.imprint","IMPRINT",EDGE,{"derivedFrom":sQuery(id+"F11.wireOp",EDGE,"E89.0")}),1.0]])]});
            extrude(context, id + "F12", {"entities" : qUnion([Q0]), "operationType" : NewBodyOperationType.REMOVE, "oppositeDirection" : true, "depth" : 12.7 * mm});
        }
        {
            var Q0;
            Q0=makeQuery(id+"F11.imprint","IMPRINT",FACE,{"disambiguationData":[TD([[makeQuery(id+"F11.imprint","IMPRINT",EDGE,{"derivedFrom":sQuery(id+"F11.wireOp",EDGE,"E125.0")}),-1.0]])]});
            extrude(context, id + "F13", {"entities" : qUnion([Q0]), "operationType" : NewBodyOperationType.REMOVE, "oppositeDirection" : true, "depth" : 12.7 * mm});
        }
        {
            var Q0;
            Q0=makeQuery(id+"F11.imprint","IMPRINT",FACE,{"disambiguationData":[TD([[makeQuery(id+"F11.imprint","IMPRINT",EDGE,{"derivedFrom":sQuery(id+"F11.wireOp",EDGE,"E127")}),-1.0]])]});
            extrude(context, id + "F14", {"entities" : qUnion([Q0]), "operationType" : NewBodyOperationType.REMOVE, "oppositeDirection" : true, "depth" : 12.7 * mm});
        }
        {
            var Q0;
            Q0=makeQuery(id+"F6.imprint","IMPRINT",FACE,{"disambiguationData":[TD([[makeQuery(id+"F6.imprint","IMPRINT",EDGE,{"derivedFrom":sQuery(id+"F6.wireOp",EDGE,"E45.0")}),-1.0]])]});
            extrude(context, id + "F15", {"entities" : qUnion([Q0]), "operationType" : NewBodyOperationType.REMOVE, "oppositeDirection" : true, "depth" : 12.7 * mm});
        }
        {
            var Q0;
            Q0=makeQuery(id+"F6.imprint","IMPRINT",FACE,{"disambiguationData":[TD([[makeQuery(id+"F6.imprint","IMPRINT",EDGE,{"derivedFrom":sQuery(id+"F6.wireOp",EDGE,"E65.0")}),1.0]])]});
            extrude(context, id + "F16", {"entities" : qUnion([Q0]), "operationType" : NewBodyOperationType.REMOVE, "oppositeDirection" : true, "depth" : 12.7 * mm});
        }
        {
            var Q0;
            Q0=makeQuery(id+"F6.imprint","IMPRINT",FACE,{"disambiguationData":[TD([[makeQuery(id+"F6.imprint","IMPRINT",EDGE,{"derivedFrom":sQuery(id+"F6.wireOp",EDGE,"E41.0")}),-1.0]])]});
            extrude(context, id + "F17", {"entities" : qUnion([Q0]), "operationType" : NewBodyOperationType.REMOVE, "oppositeDirection" : true, "depth" : 12.7 * mm});
        }
        {
            var Q0;
            Q0 = qSketchRegion(id + "F2", true);
            extrude(context, id + "F18", {"entities" : qUnion([Q0]), "operationType" : NewBodyOperationType.REMOVE, "oppositeDirection" : true, "depth" : 6.35 * mm});
        }
        {
            var Q0;
            Q0=makeQuery(id+"F1.opExtrude","CAP_EDGE",EDGE,{"disambiguationData":[OSD([sQuery(id+"F0.wireOp",EDGE,"E0.right")])],"isStart":false});
            var Q1;
            Q1=makeQuery(id+"F1.opExtrude","CAP_EDGE",EDGE,{"disambiguationData":[OSD([sQuery(id+"F0.wireOp",EDGE,"E0.right")])],"isStart":true});
            var Q2;
            Q2=makeQuery(id+"F1.opExtrude","CAP_EDGE",EDGE,{"disambiguationData":[OSD([sQuery(id+"F0.wireOp",EDGE,"E0.left")])],"isStart":true});
            var Q3;
            Q3=makeQuery(id+"F1.opExtrude","CAP_EDGE",EDGE,{"disambiguationData":[OSD([sQuery(id+"F0.wireOp",EDGE,"E0.top")])],"isStart":true});
            var Q4;
            Q4=makeQuery(id+"F1.opExtrude","SWEPT_EDGE",EDGE,{"disambiguationData":[OSD([sQuery(id+"F0.wireOp",EDGE,"E0.top"),sQuery(id+"F0.wireOp",EDGE,"E0.left")])]});
            var Q5;
            Q5=makeQuery(id+"F1.opExtrude","SWEPT_EDGE",EDGE,{"disambiguationData":[OSD([sQuery(id+"F0.wireOp",EDGE,"E0.top"),sQuery(id+"F0.wireOp",EDGE,"E0.right")])]});
            var Q6;
            Q6=makeQuery(id+"F1.opExtrude","CAP_EDGE",EDGE,{"disambiguationData":[OSD([sQuery(id+"F0.wireOp",EDGE,"E0.top")])],"isStart":false});
            var Q7;
            Q7=makeQuery(id+"F1.opExtrude","CAP_EDGE",EDGE,{"disambiguationData":[OSD([sQuery(id+"F0.wireOp",EDGE,"E0.left")])],"isStart":false});
            var Q8;
            Q8=makeQuery(id+"F1.opExtrude","CAP_EDGE",EDGE,{"disambiguationData":[OSD([sQuery(id+"F0.wireOp",EDGE,"E0.bottom")])],"isStart":false});
            var Q9;
            Q9=makeQuery(id+"F1.opExtrude","SWEPT_EDGE",EDGE,{"disambiguationData":[OSD([sQuery(id+"F0.wireOp",EDGE,"E0.bottom"),sQuery(id+"F0.wireOp",EDGE,"E0.left")])]});
            var Q10;
            Q10=makeQuery(id+"F1.opExtrude","SWEPT_EDGE",EDGE,{"disambiguationData":[OSD([sQuery(id+"F0.wireOp",EDGE,"E0.bottom"),sQuery(id+"F0.wireOp",EDGE,"E0.right")])]});
            var Q11;
            Q11=makeQuery(id+"F1.opExtrude","CAP_EDGE",EDGE,{"disambiguationData":[OSD([sQuery(id+"F0.wireOp",EDGE,"E0.bottom")])],"isStart":true});
            fillet(context, id + "F19", {"entities" : qUnion([Q0, Q1, Q2, Q3, Q4, Q5, Q6, Q7, Q8, Q9, Q10, Q11]), "radius" : 3.8 * mm, "tangentPropagation" : true, "allowEdgeOverflow" : false});
        }
    });
